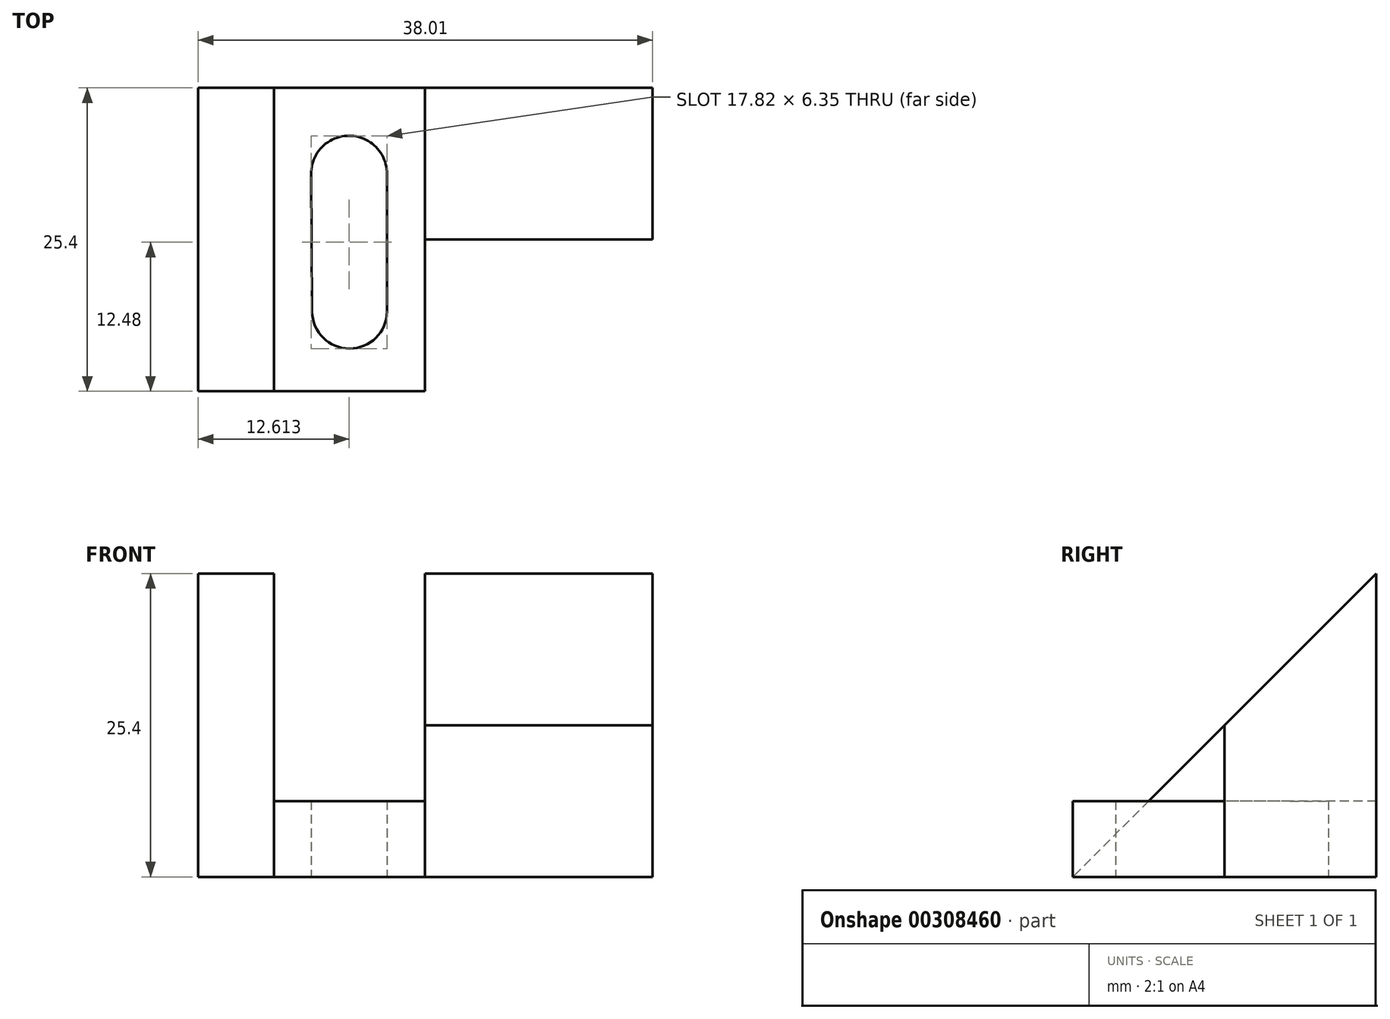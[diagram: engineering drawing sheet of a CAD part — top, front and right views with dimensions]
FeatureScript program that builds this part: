
annotation { "Feature Type Name" : "Feature", "Feature Type Description" : "" }
export const myFeature = defineFeature(function(context is Context, id is Id, definition is map)
    precondition{}
    {
        {
            var Q0;
            Q0=qCreatedBy(makeId("Top.planeOp"),FACE);
            var sketch = newSketch(context, id + "F0", { "sketchPlane" : qUnion([Q0])});
            skLineSegment(sketch, "E0", {"start": v(0, 0) * mm, "end": v(38.01, 0) * mm});
            skLineSegment(sketch, "E1", {"start": v(38.01, 0) * mm, "end": v(38.01, -12.7) * mm});
            skLineSegment(sketch, "E2", {"start": v(38.01, -12.7) * mm, "end": v(18.96, -12.7) * mm});
            skLineSegment(sketch, "E3", {"start": v(18.96, -12.7) * mm, "end": v(18.96, -25.4) * mm});
            skLineSegment(sketch, "E4", {"start": v(18.96, -25.4) * mm, "end": v(0, -25.4) * mm});
            skLineSegment(sketch, "E5", {"start": v(0, -25.4) * mm, "end": v(0, 0) * mm});
            skLineSegment(sketch, "E6", {"start": v(6.35, 0) * mm, "end": v(6.35, -25.4) * mm});
            skLineSegment(sketch, "E7", {"start": v(15.79, -7.2) * mm, "end": v(15.79, -18.72) * mm});
            skLineSegment(sketch, "E8", {"start": v(9.53, -18.72) * mm, "end": v(9.44, -7.2) * mm});
            skArc(sketch, "E9", {"start": v(15.79, -7.2) * mm, "mid": v(12.61, -4) * mm, "end": v(9.44, -7.2) * mm});
            skArc(sketch, "E10", {"start": v(9.53, -18.72) * mm, "mid": v(12.66, -21.83) * mm, "end": v(15.79, -18.72) * mm});
            skLineSegment(sketch, "E11", {"start": v(18.96, -12.7) * mm, "end": v(18.96, 0) * mm});
            skSolve(sketch);
        }
        {
            var Q0;
            {var subQ0=sQuery(id+"F0.wireOp",EDGE,"E5");Q0=makeQuery(id+"F0.imprint","IMPRINT",FACE,{"disambiguationData":[TD([[makeQuery(id+"F0.imprint","IMPRINT",EDGE,{"derivedFrom":subQ0}),-1.0]])]});}
            extrude(context, id + "F1", {"entities" : qUnion([Q0]), "depth" : 25.4 * mm});
        }
        {
            var Q0;
            {var subQ1=sQuery(id+"F0.wireOp",EDGE,"E3");Q0=makeQuery(id+"F0.imprint","IMPRINT",FACE,{"disambiguationData":[TD([[makeQuery(id+"F0.imprint","IMPRINT",EDGE,{"derivedFrom":subQ1}),-1.0]])]});}
            extrude(context, id + "F2", {"entities" : qUnion([Q0]), "operationType" : NewBodyOperationType.ADD, "depth" : 6.35 * mm});
        }
        {
            var Q0;
            {var subQ0=sQuery(id+"F0.wireOp",EDGE,"E1");Q0=makeQuery(id+"F0.imprint","IMPRINT",FACE,{"disambiguationData":[TD([[makeQuery(id+"F0.imprint","IMPRINT",EDGE,{"derivedFrom":subQ0}),-1.0]])]});}
            extrude(context, id + "F3", {"entities" : qUnion([Q0]), "operationType" : NewBodyOperationType.ADD, "depth" : 25.4 * mm});
        }
        {
            var Q0;
            Q0=makeQuery(id+"F3.opExtrude","SWEPT_FACE",FACE,{"disambiguationData":[OSD([sQuery(id+"F0.wireOp",EDGE,"E1")])]});
            var sketch = newSketch(context, id + "F4", { "sketchPlane" : qUnion([Q0])});
            skLineSegment(sketch, "E12", {"start": v(-12.7, 0) * mm, "end": v(-12.7, 25.4) * mm});
            skLineSegment(sketch, "E13", {"start": v(-12.7, 25.4) * mm, "end": v(0, 25.4) * mm});
            skLineSegment(sketch, "E14", {"start": v(0, 25.4) * mm, "end": v(0, 0) * mm});
            skLineSegment(sketch, "E15", {"start": v(0, 0) * mm, "end": v(-12.7, 0) * mm});
            skLineSegment(sketch, "E16", {"start": v(-12.7, 12.7) * mm, "end": v(0, 25.4) * mm});
            skSolve(sketch);
        }
        {
            var Q0;
            {var subQ0=sQuery(id+"F4.wireOp",EDGE,"E13");Q0=makeQuery(id+"F4.imprint","IMPRINT",FACE,{"disambiguationData":[TD([[makeQuery(id+"F4.imprint","IMPRINT",EDGE,{"derivedFrom":subQ0}),1.0]])]});}
            extrude(context, id + "F5", {"entities" : qUnion([Q0]), "operationType" : NewBodyOperationType.REMOVE, "oppositeDirection" : true, "depth" : 25.4 * mm});
        }
        {
            var Q0;
            Q0=makeQuery(id+"F1.opExtrude","SWEPT_FACE",FACE,{"disambiguationData":[OSD([sQuery(id+"F0.wireOp",EDGE,"E6")])]});
            var sketch = newSketch(context, id + "F6", { "sketchPlane" : qUnion([Q0])});
            skLineSegment(sketch, "E17", {"start": v(-25.4, 25.4) * mm, "end": v(0, 25.4) * mm});
            skLineSegment(sketch, "E18", {"start": v(0, 25.4) * mm, "end": v(-19.05, 6.35) * mm});
            skLineSegment(sketch, "E19", {"start": v(-19.05, 6.35) * mm, "end": v(-25.4, 6.35) * mm});
            skLineSegment(sketch, "E20", {"start": v(-25.4, 6.35) * mm, "end": v(-25.4, 25.4) * mm});
            skSolve(sketch);
        }
        {
            var Q0;
            Q0 = qSketchRegion(id + "F6", true);
            extrude(context, id + "F7", {"entities" : qUnion([Q0]), "operationType" : NewBodyOperationType.REMOVE, "oppositeDirection" : true, "depth" : 25.4 * mm});
        }
        {
            var Q0;
            Q0=makeQuery(id+"F1.opExtrude","SWEPT_FACE",FACE,{"disambiguationData":[OSD([sQuery(id+"F0.wireOp",EDGE,"E5")])]});
            var sketch = newSketch(context, id + "F8", { "sketchPlane" : qUnion([Q0])});
            skLineSegment(sketch, "E21", {"start": v(19.05, 6.35) * mm, "end": v(25.4, 0) * mm});
            skSolve(sketch);
        }
        {
            var Q0;
            Q0=makeQuery(id+"F8.imprint","IMPRINT",FACE,{"disambiguationData":[TD([[makeQuery(id+"F8.imprint","IMPRINT",EDGE,{"derivedFrom":sQuery(id+"F8.wireOp",EDGE,"E21")}),1.0]])]});
            extrude(context, id + "F9", {"entities" : qUnion([Q0]), "operationType" : NewBodyOperationType.REMOVE, "oppositeDirection" : true, "depth" : 6.35 * mm});
        }
    });
